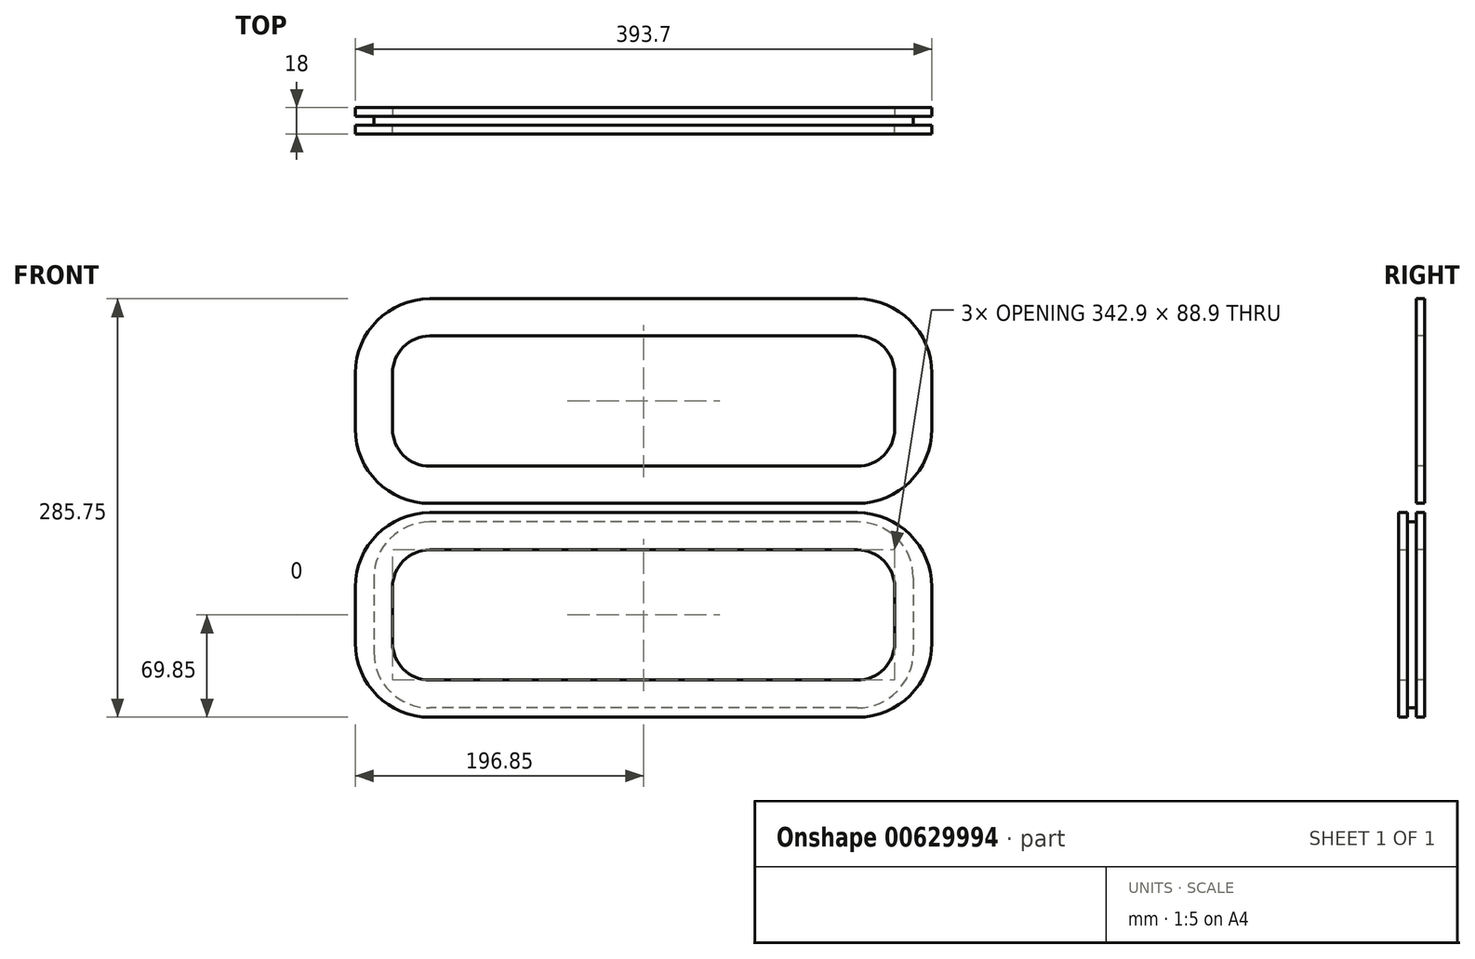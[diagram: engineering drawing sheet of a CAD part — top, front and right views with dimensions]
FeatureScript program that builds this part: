
annotation { "Feature Type Name" : "Feature", "Feature Type Description" : "" }
export const myFeature = defineFeature(function(context is Context, id is Id, definition is map)
    precondition{}
    {
        {
            var Q0;
            Q0=qCreatedBy(makeId("Front.planeOp"),FACE);
            var sketch = newSketch(context, id + "F0", { "sketchPlane" : qUnion([Q0])});
            skLineSegment(sketch, "E0.bottom", {"start": v(146.05, 63.5) * mm, "end": v(-146.05, 63.5) * mm});
            skLineSegment(sketch, "E0.top", {"start": v(146.05, -63.5) * mm, "end": v(-146.05, -63.5) * mm});
            skLineSegment(sketch, "E0.left", {"start": v(184.15, 25.4) * mm, "end": v(184.15, -25.4) * mm});
            skLineSegment(sketch, "E0.right", {"start": v(-184.15, 25.4) * mm, "end": v(-184.15, -25.4) * mm});
            skPoint(sketch, "E1.visualSharp", {"position": v(-184.15, 63.5) * mm});
            skArc(sketch, "E1.filletArc", {"start": v(-146.05, 63.5) * mm, "mid": v(-173, 52.34) * mm, "end": v(-184.15, 25.4) * mm});
            skPoint(sketch, "E2.visualSharp", {"position": v(184.15, 63.5) * mm});
            skArc(sketch, "E2.filletArc", {"start": v(184.15, 25.4) * mm, "mid": v(173, 52.34) * mm, "end": v(146.05, 63.5) * mm});
            skPoint(sketch, "E3.visualSharp", {"position": v(184.15, -63.5) * mm});
            skArc(sketch, "E3.filletArc", {"start": v(146.05, -63.5) * mm, "mid": v(173, -52.34) * mm, "end": v(184.15, -25.4) * mm});
            skPoint(sketch, "E4.visualSharp", {"position": v(-184.15, -63.5) * mm});
            skArc(sketch, "E4.filletArc", {"start": v(-184.15, -25.4) * mm, "mid": v(-173, -52.34) * mm, "end": v(-146.05, -63.5) * mm});
            skSolve(sketch);
        }
        {
            var Q0;
            Q0=makeQuery(id+"F0.imprint","IMPRINT",FACE,{"disambiguationData":[TD([[makeQuery(id+"F0.imprint","IMPRINT",EDGE,{"derivedFrom":sQuery(id+"F0.wireOp",EDGE,"E0.bottom")}),1.0]])]});
            extrude(context, id + "F1", {"entities" : qUnion([Q0]), "oppositeDirection" : true, "depth" : 6 * mm, "offsetDistance" : 25.4 * mm});
        }
        {
            var Q0;
            Q0=qCreatedBy(makeId("Front.planeOp"),FACE);
            var sketch = newSketch(context, id + "F2", { "sketchPlane" : qUnion([Q0])});
            skLineSegment(sketch, "E5.bottom", {"start": v(146.05, 69.85) * mm, "end": v(-146.05, 69.85) * mm});
            skLineSegment(sketch, "E5.top", {"start": v(146.05, -69.85) * mm, "end": v(-146.05, -69.85) * mm});
            skLineSegment(sketch, "E5.left", {"start": v(196.85, 19.05) * mm, "end": v(196.85, -19.05) * mm});
            skLineSegment(sketch, "E5.right", {"start": v(-196.85, 19.05) * mm, "end": v(-196.85, -19.05) * mm});
            skPoint(sketch, "E5.middle", {"position": v(0, 0) * mm});
            skPoint(sketch, "E6.visualSharp", {"position": v(-196.85, 69.85) * mm});
            skArc(sketch, "E6.filletArc", {"start": v(-146.05, 69.85) * mm, "mid": v(-181.97, 54.97) * mm, "end": v(-196.85, 19.05) * mm});
            skPoint(sketch, "E7.visualSharp", {"position": v(196.85, 69.85) * mm});
            skArc(sketch, "E7.filletArc", {"start": v(196.85, 19.05) * mm, "mid": v(181.97, 54.97) * mm, "end": v(146.05, 69.85) * mm});
            skPoint(sketch, "E8.visualSharp", {"position": v(196.85, -69.85) * mm});
            skArc(sketch, "E8.filletArc", {"start": v(146.05, -69.85) * mm, "mid": v(181.97, -54.97) * mm, "end": v(196.85, -19.05) * mm});
            skPoint(sketch, "E9.visualSharp", {"position": v(-196.85, -69.85) * mm});
            skArc(sketch, "E9.filletArc", {"start": v(-196.85, -19.05) * mm, "mid": v(-181.97, -54.97) * mm, "end": v(-146.05, -69.85) * mm});
            skLineSegment(sketch, "E10.bottom", {"start": v(146.05, 44.45) * mm, "end": v(-146.05, 44.45) * mm});
            skLineSegment(sketch, "E10.top", {"start": v(146.05, -44.45) * mm, "end": v(-146.05, -44.45) * mm});
            skLineSegment(sketch, "E10.left", {"start": v(171.45, 19.05) * mm, "end": v(171.45, -19.05) * mm});
            skLineSegment(sketch, "E10.right", {"start": v(-171.45, 19.05) * mm, "end": v(-171.45, -19.05) * mm});
            skPoint(sketch, "E11.visualSharp", {"position": v(-171.45, 44.45) * mm});
            skArc(sketch, "E11.filletArc", {"start": v(-146.05, 44.45) * mm, "mid": v(-164.01, 37.01) * mm, "end": v(-171.45, 19.05) * mm});
            skPoint(sketch, "E12.visualSharp", {"position": v(-171.45, -44.45) * mm});
            skArc(sketch, "E12.filletArc", {"start": v(-171.45, -19.05) * mm, "mid": v(-164.01, -37.01) * mm, "end": v(-146.05, -44.45) * mm});
            skPoint(sketch, "E13.visualSharp", {"position": v(171.45, -44.45) * mm});
            skArc(sketch, "E13.filletArc", {"start": v(146.05, -44.45) * mm, "mid": v(164.01, -37.01) * mm, "end": v(171.45, -19.05) * mm});
            skPoint(sketch, "E14.visualSharp", {"position": v(171.45, 44.45) * mm});
            skArc(sketch, "E14.filletArc", {"start": v(171.45, 19.05) * mm, "mid": v(164.01, 37.01) * mm, "end": v(146.05, 44.45) * mm});
            skArc(sketch, "E15.0.1.0", {"start": v(146.05, 101.6) * mm, "mid": v(164.01, 109.04) * mm, "end": v(171.45, 127) * mm});
            skPoint(sketch, "E15.0.1.1", {"position": v(-196.85, 215.9) * mm});
            skLineSegment(sketch, "E15.0.1.2", {"start": v(146.05, 215.9) * mm, "end": v(-146.05, 215.9) * mm});
            skLineSegment(sketch, "E15.0.1.3", {"start": v(-196.85, 165.1) * mm, "end": v(-196.85, 127) * mm});
            skPoint(sketch, "E15.0.1.4", {"position": v(196.85, 215.9) * mm});
            skLineSegment(sketch, "E15.0.1.5", {"start": v(146.05, 101.6) * mm, "end": v(-146.05, 101.6) * mm});
            skArc(sketch, "E15.0.1.6", {"start": v(-196.85, 127) * mm, "mid": v(-181.97, 91.08) * mm, "end": v(-146.05, 76.2) * mm});
            skPoint(sketch, "E15.0.1.7", {"position": v(-171.45, 101.6) * mm});
            skPoint(sketch, "E15.0.1.8", {"position": v(171.45, 101.6) * mm});
            skLineSegment(sketch, "E15.0.1.9", {"start": v(-171.45, 165.1) * mm, "end": v(-171.45, 127) * mm});
            skLineSegment(sketch, "E15.0.1.10", {"start": v(171.45, 165.1) * mm, "end": v(171.45, 127) * mm});
            skPoint(sketch, "E15.0.1.11", {"position": v(-196.85, 76.2) * mm});
            skArc(sketch, "E15.0.1.12", {"start": v(-171.45, 127) * mm, "mid": v(-164.01, 109.04) * mm, "end": v(-146.05, 101.6) * mm});
            skPoint(sketch, "E15.0.1.13", {"position": v(196.85, 76.2) * mm});
            skLineSegment(sketch, "E15.0.1.14", {"start": v(146.05, 76.2) * mm, "end": v(-146.05, 76.2) * mm});
            skArc(sketch, "E15.0.1.15", {"start": v(146.05, 76.2) * mm, "mid": v(181.97, 91.08) * mm, "end": v(196.85, 127) * mm});
            skPoint(sketch, "E15.0.1.16", {"position": v(171.45, 190.5) * mm});
            skPoint(sketch, "E15.0.1.17", {"position": v(-171.45, 190.5) * mm});
            skLineSegment(sketch, "E15.0.1.18", {"start": v(146.05, 190.5) * mm, "end": v(-146.05, 190.5) * mm});
            skArc(sketch, "E15.0.1.19", {"start": v(-146.05, 215.9) * mm, "mid": v(-181.97, 201.02) * mm, "end": v(-196.85, 165.1) * mm});
            skArc(sketch, "E15.0.1.20", {"start": v(-146.05, 190.5) * mm, "mid": v(-164.01, 183.06) * mm, "end": v(-171.45, 165.1) * mm});
            skArc(sketch, "E15.0.1.21", {"start": v(171.45, 165.1) * mm, "mid": v(164.01, 183.06) * mm, "end": v(146.05, 190.5) * mm});
            skArc(sketch, "E15.0.1.22", {"start": v(196.85, 165.1) * mm, "mid": v(181.97, 201.02) * mm, "end": v(146.05, 215.9) * mm});
            skPoint(sketch, "E15.0.1.23", {"position": v(0, 146.05) * mm});
            skLineSegment(sketch, "E15.0.1.24", {"start": v(196.85, 165.1) * mm, "end": v(196.85, 127) * mm});
            skPoint(sketch, "E15.0.1.25", {"position": v(0, 146.05) * mm});
            skLineSegment(sketch, "E15.direction1", {"start": v(-196.85, -69.85) * mm, "end": v(-171.45, -69.85) * mm, "construction": true});
            skLineSegment(sketch, "E15.direction2", {"start": v(-196.85, -69.85) * mm, "end": v(-196.85, 76.2) * mm, "construction": true});
            skSolve(sketch);
        }
        {
            var Q0;
            Q0=makeQuery(id+"F2.imprint","IMPRINT",FACE,{"disambiguationData":[TD([[makeQuery(id+"F2.imprint","IMPRINT",EDGE,{"derivedFrom":sQuery(id+"F2.wireOp",EDGE,"E5.bottom")}),1.0]])]});
            extrude(context, id + "F3", {"entities" : qUnion([Q0]), "depth" : 6 * mm, "offsetDistance" : 25.4 * mm});
        }
        {
            var Q0;
            Q0 = qSketchRegion(id + "F2", true);
            extrude(context, id + "F4", {"entities" : qUnion([Q0]), "oppositeDirection" : true, "depth" : 12 * mm, "offsetDistance" : 25.4 * mm, "hasSecondDirection" : true, "secondDirectionOppositeDirection" : true, "secondDirectionDepth" : 6 * mm});
        }
    });
